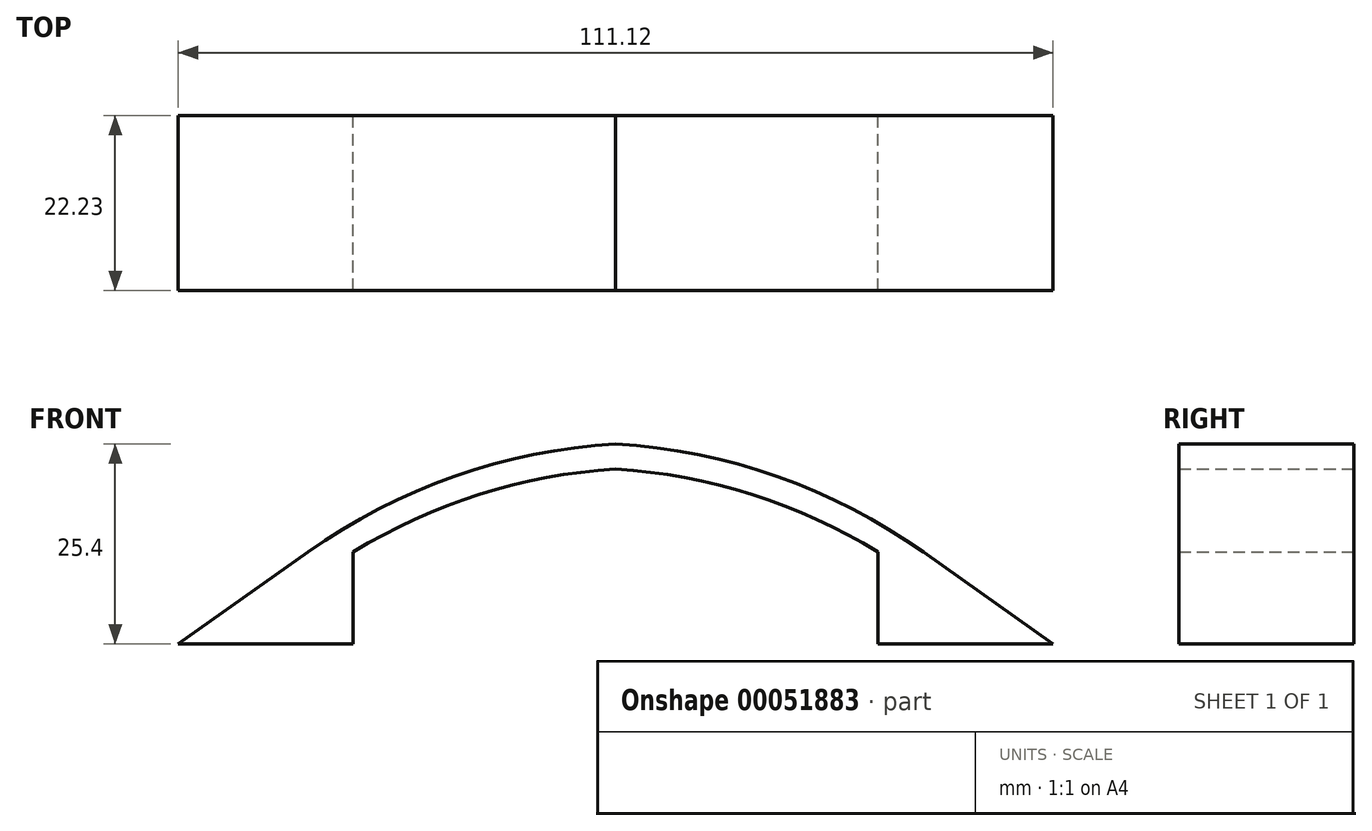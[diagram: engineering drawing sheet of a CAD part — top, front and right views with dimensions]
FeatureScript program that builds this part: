
annotation { "Feature Type Name" : "Feature", "Feature Type Description" : "" }
export const myFeature = defineFeature(function(context is Context, id is Id, definition is map)
    precondition{}
    {
        {
            var Q0;
            Q0=qCreatedBy(makeId("Front.planeOp"),FACE);
            var sketch = newSketch(context, id + "F0", { "sketchPlane" : qUnion([Q0])});
            skLineSegment(sketch, "E0", {"start": v(-55.56, 0) * mm, "end": v(-33.34, 0) * mm});
            skLineSegment(sketch, "E1", {"start": v(-33.34, 0) * mm, "end": v(-33.34, 11.67) * mm});
            skLineSegment(sketch, "E2", {"start": v(-55.56, 0) * mm, "end": v(-39.08, 11.67) * mm});
            skArc(sketch, "E3", {"start": v(0, 22.23) * mm, "mid": v(-17.32, 19) * mm, "end": v(-33.34, 11.67) * mm});
            skArc(sketch, "E4", {"start": v(0, 25.4) * mm, "mid": v(-20.5, 21.27) * mm, "end": v(-39.08, 11.67) * mm});
            skLineSegment(sketch, "E5", {"start": v(33.34, 0) * mm, "end": v(55.56, 0) * mm});
            skLineSegment(sketch, "E6", {"start": v(55.56, 0) * mm, "end": v(39.08, 11.67) * mm});
            skLineSegment(sketch, "E7", {"start": v(33.34, 0) * mm, "end": v(33.34, 11.67) * mm});
            skArc(sketch, "E8", {"start": v(33.34, 11.67) * mm, "mid": v(17.32, 19) * mm, "end": v(0, 22.22) * mm});
            skArc(sketch, "E9", {"start": v(39.08, 11.67) * mm, "mid": v(20.5, 21.27) * mm, "end": v(0, 25.4) * mm});
            skSolve(sketch);
        }
        {
            var Q0;
            Q0=makeQuery(id+"F0.imprint","IMPRINT",FACE,{"disambiguationData":[TD([[makeQuery(id+"F0.imprint","IMPRINT",EDGE,{"derivedFrom":sQuery(id+"F0.wireOp",EDGE,"E0")}),1.0]])]});
            extrude(context, id + "F1", {"entities" : qUnion([Q0]), "depth" : 22.22 * mm});
        }
    });
